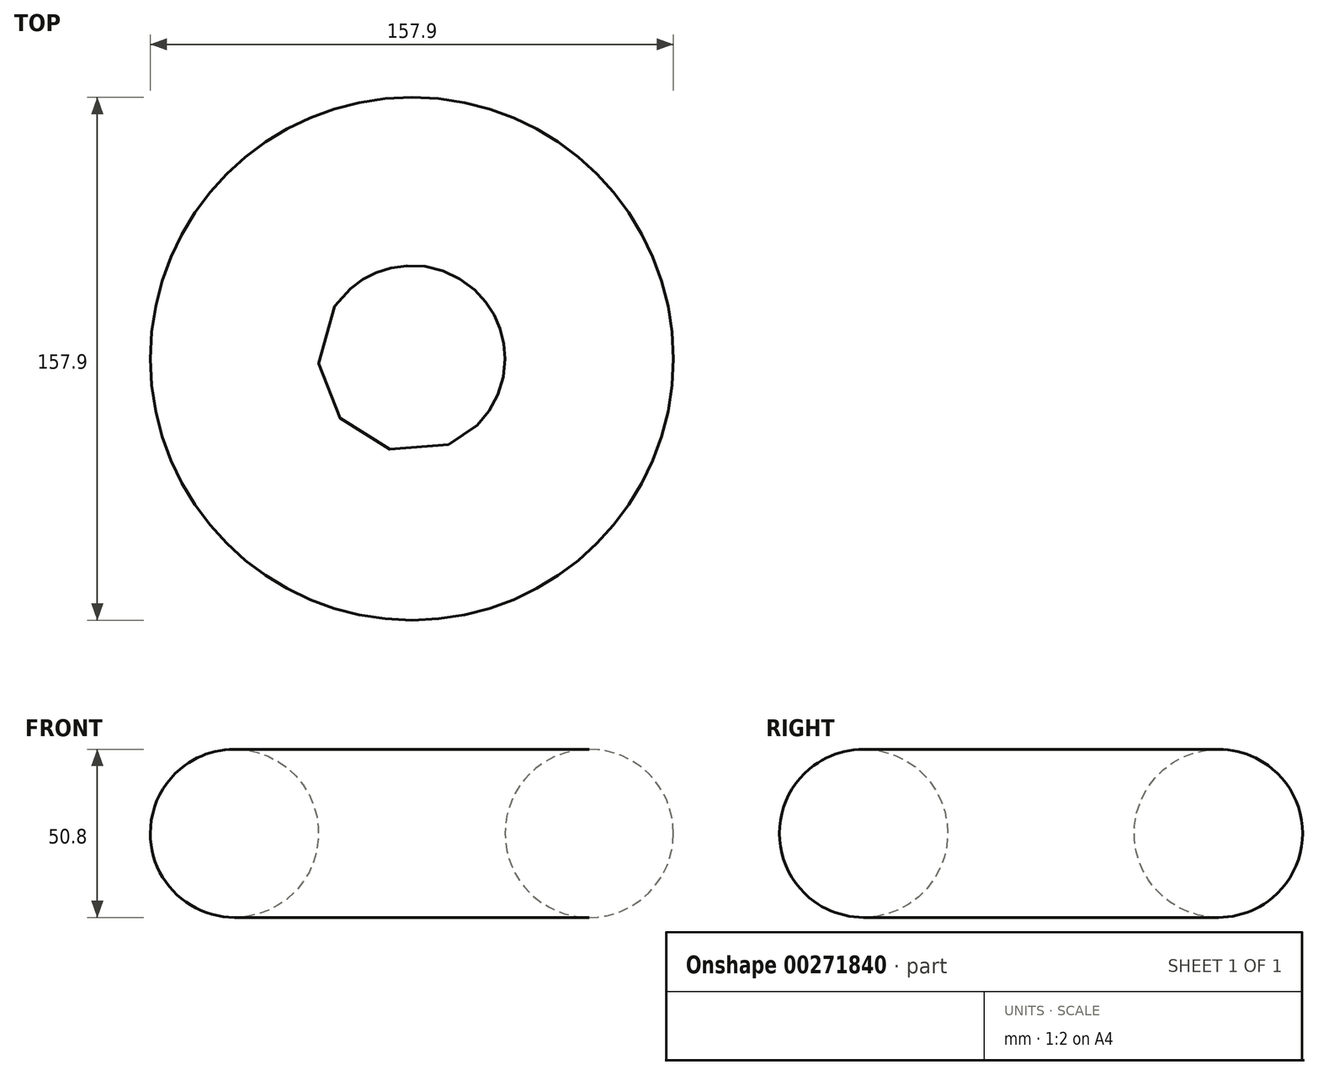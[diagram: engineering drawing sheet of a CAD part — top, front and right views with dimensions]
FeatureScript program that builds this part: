
annotation { "Feature Type Name" : "Feature", "Feature Type Description" : "" }
export const myFeature = defineFeature(function(context is Context, id is Id, definition is map)
    precondition{}
    {
        {
            var Q0;
            Q0=qCreatedBy(makeId("Front.planeOp"),FACE);
            var sketch = newSketch(context, id + "F0", { "sketchPlane" : qUnion([Q0])});
            skCircle(sketch, "E0", {"center": v(-53.55, 0) * mm, "radius": 25.4 * mm});
            skLineSegment(sketch, "E1", {"start": v(0, 50.94) * mm, "end": v(0, -76.06) * mm, "construction": true});
            skSolve(sketch);
        }
        {
            var Q0;
            Q0 = qSketchRegion(id + "F0", true);
            var Q1;
            Q1=sQuery(id+"F0.wireOp",EDGE,"E1");
            revolve(context, id + "F1", {"entities" : qUnion([Q0]), "axis" : qUnion([Q1]), "revolveType" : RevolveType.FULL});
        }
    });
